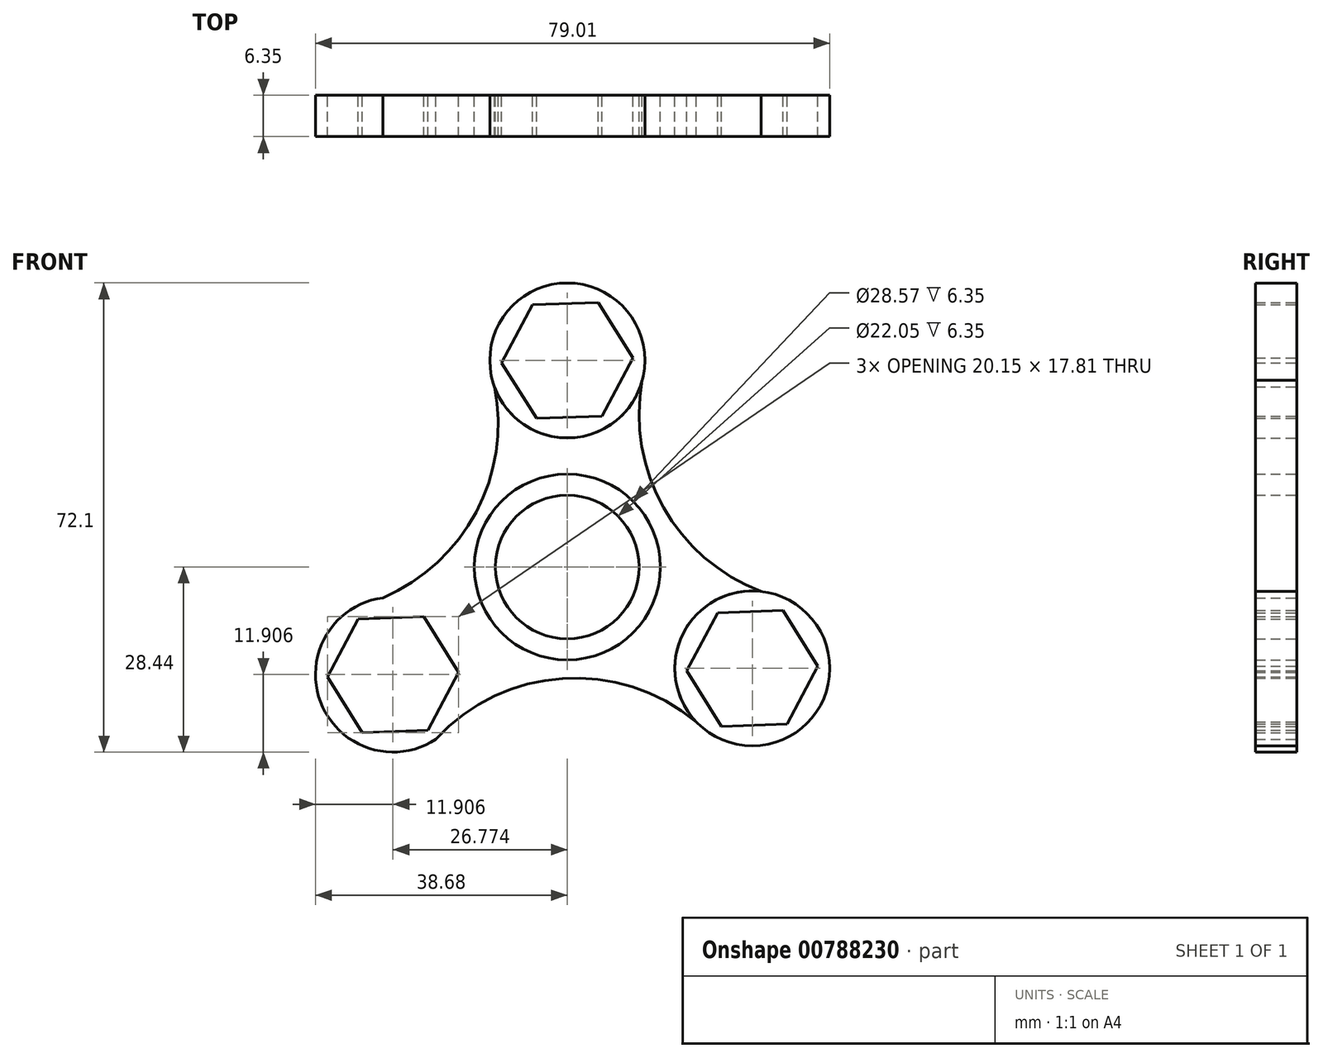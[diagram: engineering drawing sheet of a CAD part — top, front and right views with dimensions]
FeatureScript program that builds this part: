
annotation { "Feature Type Name" : "Feature", "Feature Type Description" : "" }
export const myFeature = defineFeature(function(context is Context, id is Id, definition is map)
    precondition{}
    {
        {
            var Q0;
            Q0=qCreatedBy(makeId("Front.planeOp"),FACE);
            var sketch = newSketch(context, id + "F0", { "sketchPlane" : qUnion([Q0])});
            skCircle(sketch, "E0", {"center": v(0, 0) * mm, "radius": 11.02 * mm});
            skCircle(sketch, "E1", {"center": v(0, 0) * mm, "radius": 14.29 * mm});
            skCircle(sketch, "E2.cCircle", {"center": v(0, 31.75) * mm, "radius": 8.73 * mm, "construction": true});
            skLineSegment(sketch, "E2.0", {"start": v(10.08, 32.1) * mm, "end": v(5.35, 23.2) * mm});
            skLineSegment(sketch, "E2.1", {"start": v(5.35, 23.2) * mm, "end": v(-4.73, 22.84) * mm});
            skLineSegment(sketch, "E2.2", {"start": v(-4.73, 22.84) * mm, "end": v(-10.08, 31.4) * mm});
            skLineSegment(sketch, "E2.3", {"start": v(-10.08, 31.4) * mm, "end": v(-5.35, 40.3) * mm});
            skLineSegment(sketch, "E2.4", {"start": v(-5.35, 40.3) * mm, "end": v(4.73, 40.66) * mm});
            skLineSegment(sketch, "E2.5", {"start": v(4.73, 40.66) * mm, "end": v(10.08, 32.1) * mm});
            skPoint(sketch, "E2.0.midPoint", {"position": v(7.71, 27.66) * mm});
            skCircle(sketch, "E3", {"center": v(0, 31.75) * mm, "radius": 11.9 * mm});
            skCircle(sketch, "E4.1.0", {"center": v(-26.77, -16.53) * mm, "radius": 11.9 * mm});
            skCircle(sketch, "E4.1.1", {"center": v(-26.77, -16.53) * mm, "radius": 8.73 * mm, "construction": true});
            skPoint(sketch, "E4.1.2", {"position": v(-27.08, -7.8) * mm});
            skLineSegment(sketch, "E4.1.3", {"start": v(-36.85, -16.9) * mm, "end": v(-32.12, -7.99) * mm});
            skLineSegment(sketch, "E4.1.4", {"start": v(-31.5, -25.44) * mm, "end": v(-36.85, -16.9) * mm});
            skLineSegment(sketch, "E4.1.5", {"start": v(-21.43, -25.08) * mm, "end": v(-31.5, -25.44) * mm});
            skLineSegment(sketch, "E4.1.6", {"start": v(-16.7, -16.18) * mm, "end": v(-21.43, -25.08) * mm});
            skLineSegment(sketch, "E4.1.7", {"start": v(-22.05, -7.63) * mm, "end": v(-16.7, -16.18) * mm});
            skLineSegment(sketch, "E4.1.8", {"start": v(-32.12, -7.99) * mm, "end": v(-22.05, -7.63) * mm});
            skCircle(sketch, "E4.2.0", {"center": v(28.43, -15.58) * mm, "radius": 11.9 * mm});
            skCircle(sketch, "E4.2.1", {"center": v(28.43, -15.58) * mm, "radius": 8.73 * mm, "construction": true});
            skPoint(sketch, "E4.2.2", {"position": v(21.03, -20.21) * mm});
            skLineSegment(sketch, "E4.2.3", {"start": v(33.78, -24.13) * mm, "end": v(23.7, -24.48) * mm});
            skLineSegment(sketch, "E4.2.4", {"start": v(38.5, -15.22) * mm, "end": v(33.78, -24.13) * mm});
            skLineSegment(sketch, "E4.2.5", {"start": v(33.16, -6.67) * mm, "end": v(38.5, -15.22) * mm});
            skLineSegment(sketch, "E4.2.6", {"start": v(23.08, -7.03) * mm, "end": v(33.16, -6.67) * mm});
            skLineSegment(sketch, "E4.2.7", {"start": v(18.35, -15.94) * mm, "end": v(23.08, -7.03) * mm});
            skLineSegment(sketch, "E4.2.8", {"start": v(23.7, -24.48) * mm, "end": v(18.35, -15.94) * mm});
            skPoint(sketch, "E4.center", {"position": v(0.55, -0.12) * mm});
            skPoint(sketch, "E5.endSnap0", {"position": v(-7.4, 27.12) * mm});
            skSolve(sketch);
        }
        {
            var Q0;
            Q0=qCreatedBy(makeId("Front.planeOp"),FACE);
            var sketch = newSketch(context, id + "F1", { "sketchPlane" : qUnion([Q0])});
            skLineSegment(sketch, "E6.0", {"start": v(23.08, -7.03) * mm, "end": v(33.16, -6.67) * mm});
            skLineSegment(sketch, "E6.1", {"start": v(33.78, -24.13) * mm, "end": v(23.7, -24.48) * mm});
            skLineSegment(sketch, "E6.2", {"start": v(33.16, -6.67) * mm, "end": v(38.5, -15.22) * mm});
            skCircle(sketch, "E6.3", {"center": v(-26.77, -16.53) * mm, "radius": 8.73 * mm});
            skLineSegment(sketch, "E6.4", {"start": v(23.7, -24.48) * mm, "end": v(18.35, -15.94) * mm});
            skLineSegment(sketch, "E6.5", {"start": v(-36.85, -16.9) * mm, "end": v(-32.12, -7.99) * mm});
            skCircle(sketch, "E6.6", {"center": v(-26.77, -16.53) * mm, "radius": 11.9 * mm});
            skCircle(sketch, "E6.7", {"center": v(0, 31.75) * mm, "radius": 11.9 * mm});
            skLineSegment(sketch, "E6.8", {"start": v(4.73, 40.66) * mm, "end": v(10.08, 32.1) * mm});
            skLineSegment(sketch, "E6.9", {"start": v(-10.08, 31.4) * mm, "end": v(-5.35, 40.3) * mm});
            skLineSegment(sketch, "E6.10", {"start": v(-5.35, 40.3) * mm, "end": v(4.73, 40.66) * mm});
            skLineSegment(sketch, "E6.11", {"start": v(-4.73, 22.84) * mm, "end": v(-10.08, 31.4) * mm});
            skLineSegment(sketch, "E6.12", {"start": v(5.35, 23.2) * mm, "end": v(-4.73, 22.84) * mm});
            skCircle(sketch, "E6.13", {"center": v(28.43, -15.58) * mm, "radius": 11.9 * mm});
            skLineSegment(sketch, "E6.14", {"start": v(10.08, 32.1) * mm, "end": v(5.35, 23.2) * mm});
            skCircle(sketch, "E6.15", {"center": v(0, 0) * mm, "radius": 14.29 * mm});
            skCircle(sketch, "E6.16", {"center": v(0, 0) * mm, "radius": 11.02 * mm});
            skLineSegment(sketch, "E6.17", {"start": v(-22.05, -7.63) * mm, "end": v(-16.7, -16.18) * mm});
            skLineSegment(sketch, "E6.18", {"start": v(-16.7, -16.18) * mm, "end": v(-21.43, -25.08) * mm});
            skLineSegment(sketch, "E6.19", {"start": v(-21.43, -25.08) * mm, "end": v(-31.5, -25.44) * mm});
            skLineSegment(sketch, "E6.20", {"start": v(-32.12, -7.99) * mm, "end": v(-22.05, -7.63) * mm});
            skLineSegment(sketch, "E6.21", {"start": v(-31.5, -25.44) * mm, "end": v(-36.85, -16.9) * mm});
            skCircle(sketch, "E6.22", {"center": v(28.43, -15.58) * mm, "radius": 8.73 * mm});
            skLineSegment(sketch, "E6.23", {"start": v(38.5, -15.22) * mm, "end": v(33.78, -24.13) * mm});
            skCircle(sketch, "E6.24", {"center": v(0, 31.75) * mm, "radius": 8.73 * mm});
            skLineSegment(sketch, "E6.25", {"start": v(18.35, -15.94) * mm, "end": v(23.08, -7.03) * mm});
            skArc(sketch, "E7", {"start": v(21.25, -25.08) * mm, "mid": v(0.23, -17.08) * mm, "end": v(-20.2, -26.47) * mm});
            skArc(sketch, "E8.1.0", {"start": v(11.84, 30.27) * mm, "mid": v(15.43, 8.07) * mm, "end": v(33.78, -4.94) * mm});
            skArc(sketch, "E8.2.0", {"start": v(-31.5, -5.87) * mm, "mid": v(-14.06, 8.34) * mm, "end": v(-11.97, 30.74) * mm});
            skSolve(sketch);
        }
        {
            var Q0;
            Q0=makeQuery(id+"F1.imprint","IMPRINT",FACE,{"disambiguationData":[TD([[makeQuery(id+"F1.imprint","IMPRINT",EDGE,{"derivedFrom":sQuery(id+"F1.wireOp",EDGE,"E6.15")}),-1.0]])]});
            var Q1;
            Q1=makeQuery(id+"F0.imprint","IMPRINT",FACE,{"disambiguationData":[TD([[makeQuery(id+"F0.imprint","IMPRINT",EDGE,{"derivedFrom":sQuery(id+"F0.wireOp",EDGE,"E0")}),-1.0]])]});
            var Q2;
            Q2=makeQuery(id+"F0.imprint","IMPRINT",FACE,{"disambiguationData":[TD([[makeQuery(id+"F0.imprint","IMPRINT",EDGE,{"derivedFrom":sQuery(id+"F0.wireOp",EDGE,"E2.0")}),1.0]])]});
            var Q3;
            {var subQ0=sQuery(id+"F1.wireOp",EDGE,"E6.21");var subQ18=sQuery(id+"F1.wireOp",EDGE,"E6.5");var subQ19=makeQuery(id+"F1.imprint","INTERSECT",VERTEX,{"derivedFrom":[subQ18,subQ0]});Q3=makeQuery(id+"F1.imprint","IMPRINT",FACE,{"disambiguationData":[TD([[makeQuery(id+"F1.imprint","IMPRINT",EDGE,{"disambiguationData":[TD([[subQ19,-1.0]])],"derivedFrom":subQ18}),1.0]])]});}
            var Q4;
            Q4=makeQuery(id+"F0.imprint","IMPRINT",FACE,{"disambiguationData":[TD([[makeQuery(id+"F0.imprint","IMPRINT",EDGE,{"derivedFrom":sQuery(id+"F0.wireOp",EDGE,"E4.2.0")}),1.0]])]});
            extrude(context, id + "F2", {"entities" : qUnion([Q0, Q1, Q2, Q3, Q4]), "depth" : 6.35 * mm, "offsetDistance" : 25.4 * mm});
        }
    });
